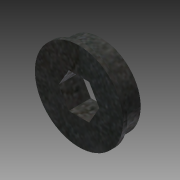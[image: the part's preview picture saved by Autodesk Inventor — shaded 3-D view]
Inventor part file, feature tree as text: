
AUTODESK INVENTOR PART (.ipt)
format: ipt  version: 2014 (Build 180170000, 170)  size: 117,248 bytes
history: native  units: in
note: dims shown in document units (in); Inventor stores cm internally (conversion verified against a paired STEP export)
features: extrude x2, sketch x2
ambient origin geometry x8: Origin, YZ Plane, XZ Plane, XY Plane, X Axis, Y Axis, Z Axis, Center Point
bodies: Solid1 (feature_tree)
feature tree (4):
  extrude  "Extrusion1"  Depth=0.5in
  extrude  "Extrusion2"  Depth=0.0625in
  sketch  "Sketch1"  dims[d0=0.5in d1=1.125in]
  sketch  "Sketch2"  dims[d2=0.25in d3=0.0in d4=0.0625in d5=0.0625in d6=0.0in]
